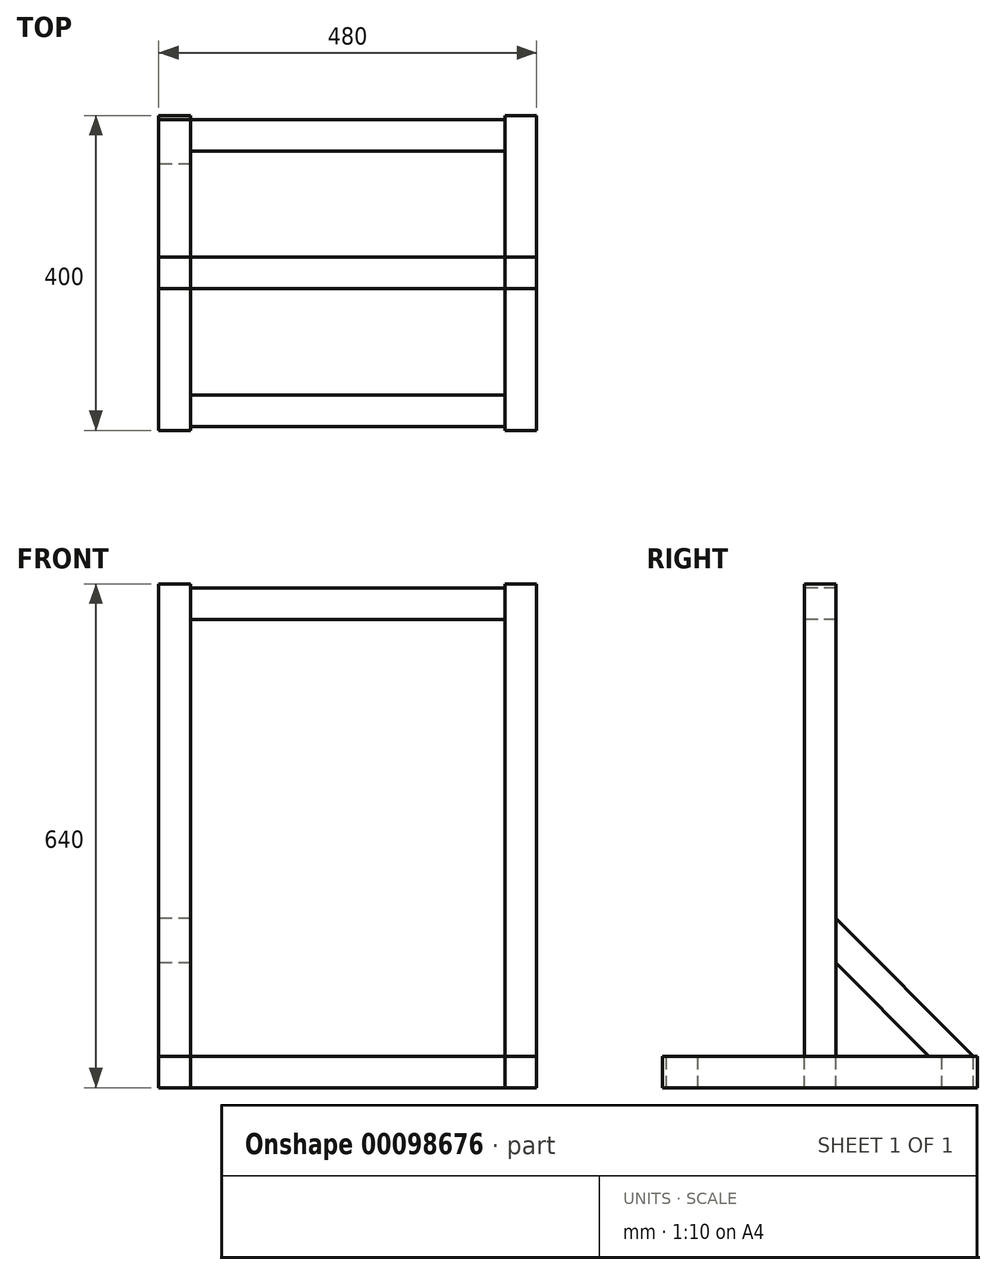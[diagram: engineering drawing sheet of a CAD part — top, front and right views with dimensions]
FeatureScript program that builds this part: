
annotation { "Feature Type Name" : "Feature", "Feature Type Description" : "" }
export const myFeature = defineFeature(function(context is Context, id is Id, definition is map)
    precondition{}
    {
        {
            assignVariable(context, id + "F0", {"name" : "height", "anyValue" : 600});
        }
        {
            var Q0;
            Q0=qCreatedBy(makeId("Top.planeOp"),FACE);
            var sketch = newSketch(context, id + "F1", { "sketchPlane" : qUnion([Q0])});
            skLineSegment(sketch, "E0.bottom", {"start": v(-240, 200) * mm, "end": v(-200, 200) * mm});
            skLineSegment(sketch, "E0.top", {"start": v(-240, -200) * mm, "end": v(-200, -200) * mm});
            skLineSegment(sketch, "E0.left", {"start": v(-240, 200) * mm, "end": v(-240, -200) * mm});
            skLineSegment(sketch, "E0.right", {"start": v(-200, 200) * mm, "end": v(-200, -200) * mm});
            skLineSegment(sketch, "E1", {"start": v(-200, 20) * mm, "end": v(0, 20) * mm});
            skLineSegment(sketch, "E2", {"start": v(-200, -20) * mm, "end": v(0, -20) * mm});
            skLineSegment(sketch, "E3", {"start": v(-200, -155) * mm, "end": v(0, -155) * mm});
            skLineSegment(sketch, "E4", {"start": v(-200, -195) * mm, "end": v(0, -195) * mm});
            skLineSegment(sketch, "E5", {"start": v(0, -195) * mm, "end": v(0, 195) * mm, "construction": true});
            skLineSegment(sketch, "E6.MirrorCS", {"start": v(200, -195) * mm, "end": v(0, -195) * mm});
            skLineSegment(sketch, "E7.MirrorCS", {"start": v(200, -155) * mm, "end": v(0, -155) * mm});
            skLineSegment(sketch, "E8.MirrorCS", {"start": v(200, 200) * mm, "end": v(200, -200) * mm});
            skLineSegment(sketch, "E9.MirrorCS", {"start": v(240, 200) * mm, "end": v(240, -200) * mm});
            skLineSegment(sketch, "E10.MirrorCS", {"start": v(240, 200) * mm, "end": v(200, 200) * mm});
            skLineSegment(sketch, "E11.MirrorCS", {"start": v(240, -200) * mm, "end": v(200, -200) * mm});
            skLineSegment(sketch, "E12.MirrorCS", {"start": v(200, -20) * mm, "end": v(0, -20) * mm});
            skLineSegment(sketch, "E13.MirrorCS", {"start": v(200, 20) * mm, "end": v(0, 20) * mm});
            skLineSegment(sketch, "E14", {"start": v(-200, 20) * mm, "end": v(-240, 20) * mm});
            skLineSegment(sketch, "E15", {"start": v(-200, -20) * mm, "end": v(-240, -20) * mm});
            skLineSegment(sketch, "E16.MirrorCS", {"start": v(200, 20) * mm, "end": v(240, 20) * mm});
            skLineSegment(sketch, "E17.MirrorCS", {"start": v(200, -20) * mm, "end": v(240, -20) * mm});
            skLineSegment(sketch, "E18", {"start": v(-240, 0) * mm, "end": v(240, 0) * mm, "construction": true});
            skLineSegment(sketch, "E19.MirrorCS", {"start": v(200, 155) * mm, "end": v(0, 155) * mm});
            skLineSegment(sketch, "E20.MirrorCS", {"start": v(200, 195) * mm, "end": v(0, 195) * mm});
            skLineSegment(sketch, "E21.MirrorCS", {"start": v(-200, 195) * mm, "end": v(0, 195) * mm});
            skLineSegment(sketch, "E22.MirrorCS", {"start": v(-200, 155) * mm, "end": v(0, 155) * mm});
            skSolve(sketch);
        }
        {
            var Q0;
            {var subQ1=sQuery(id+"F1.wireOp",EDGE,"E0.bottom");Q0=makeQuery(id+"F1.imprint","IMPRINT",FACE,{"disambiguationData":[TD([[makeQuery(id+"F1.imprint","IMPRINT",EDGE,{"derivedFrom":subQ1}),-1.0]])]});}
            var Q1;
            Q1=makeQuery(id+"F1.imprint","IMPRINT",FACE,{"disambiguationData":[TD([[makeQuery(id+"F1.imprint","IMPRINT",EDGE,{"derivedFrom":sQuery(id+"F1.wireOp",EDGE,"E9.MirrorCS")}),-1.0]])]});
            var Q2;
            {var subQ0=sQuery(id+"F1.wireOp",EDGE,"E14");Q2=makeQuery(id+"F1.imprint","IMPRINT",FACE,{"disambiguationData":[TD([[makeQuery(id+"F1.imprint","IMPRINT",EDGE,{"derivedFrom":subQ0}),1.0]])]});}
            var Q3;
            {var subQ3=sQuery(id+"F1.wireOp",EDGE,"E0.top");Q3=makeQuery(id+"F1.imprint","IMPRINT",FACE,{"disambiguationData":[TD([[makeQuery(id+"F1.imprint","IMPRINT",EDGE,{"derivedFrom":subQ3}),1.0]])]});}
            var Q4;
            {var subQ2=sQuery(id+"F1.wireOp",EDGE,"E11.MirrorCS");Q4=makeQuery(id+"F1.imprint","IMPRINT",FACE,{"disambiguationData":[TD([[makeQuery(id+"F1.imprint","IMPRINT",EDGE,{"derivedFrom":subQ2}),-1.0]])]});}
            var Q5;
            {var subQ0=sQuery(id+"F1.wireOp",EDGE,"E10.MirrorCS");Q5=makeQuery(id+"F1.imprint","IMPRINT",FACE,{"disambiguationData":[TD([[makeQuery(id+"F1.imprint","IMPRINT",EDGE,{"derivedFrom":subQ0}),1.0]])]});}
            extrude(context, id + "F2", {"entities" : qUnion([Q0, Q1, Q2, Q3, Q4, Q5]), "oppositeDirection" : true, "depth" : 40 * mm});
        }
        {
            var Q0;
            {var subQ4=sQuery(id+"F1.wireOp",EDGE,"E1");Q0=makeQuery(id+"F1.imprint","IMPRINT",FACE,{"disambiguationData":[TD([[makeQuery(id+"F1.imprint","IMPRINT",EDGE,{"derivedFrom":subQ4}),-1.0]])]});}
            var Q1;
            {var subQ2=sQuery(id+"F1.wireOp",EDGE,"E3");Q1=makeQuery(id+"F1.imprint","IMPRINT",FACE,{"disambiguationData":[TD([[makeQuery(id+"F1.imprint","IMPRINT",EDGE,{"derivedFrom":subQ2}),-1.0]])]});}
            var Q2;
            {var subQ4=sQuery(id+"F1.wireOp",EDGE,"E19.MirrorCS");Q2=makeQuery(id+"F1.imprint","IMPRINT",FACE,{"disambiguationData":[TD([[makeQuery(id+"F1.imprint","IMPRINT",EDGE,{"derivedFrom":subQ4}),-1.0]])]});}
            extrude(context, id + "F3", {"entities" : qUnion([Q0, Q1, Q2]), "oppositeDirection" : true, "depth" : 40 * mm});
        }
        {
            var Q0;
            {var subQ0=sQuery(id+"F1.wireOp",EDGE,"E14");Q0=makeQuery(id+"F1.imprint","IMPRINT",FACE,{"disambiguationData":[TD([[makeQuery(id+"F1.imprint","IMPRINT",EDGE,{"derivedFrom":subQ0}),1.0]])]});}
            var Q1;
            {var subQ2=sQuery(id+"F1.wireOp",EDGE,"E16.MirrorCS");Q1=makeQuery(id+"F1.imprint","IMPRINT",FACE,{"disambiguationData":[TD([[makeQuery(id+"F1.imprint","IMPRINT",EDGE,{"derivedFrom":subQ2}),-1.0]])]});}
            extrude(context, id + "F4", {"entities" : qUnion([Q0, Q1]), "depth" : (getVariable(context, 'height')) * mm});
        }
        {
            var Q0;
            Q0=makeQuery(id+"F4.opExtrude","SWEPT_FACE",FACE,{"disambiguationData":[OSD([sQuery(id+"F1.wireOp",EDGE,"E15")])]});
            var sketch = newSketch(context, id + "F5", { "sketchPlane" : qUnion([Q0])});
            skLineSegment(sketch, "E23.bottom", {"start": v(-200, 595) * mm, "end": v(200, 595) * mm});
            skLineSegment(sketch, "E23.top", {"start": v(-200, 555) * mm, "end": v(200, 555) * mm});
            skLineSegment(sketch, "E23.left", {"start": v(-200, 595) * mm, "end": v(-200, 555) * mm});
            skLineSegment(sketch, "E23.right", {"start": v(200, 595) * mm, "end": v(200, 555) * mm});
            skSolve(sketch);
        }
        {
            var Q0;
            Q0=makeQuery(id+"F5.imprint","IMPRINT",FACE,{"disambiguationData":[TD([[makeQuery(id+"F5.imprint","IMPRINT",EDGE,{"derivedFrom":sQuery(id+"F5.wireOp",EDGE,"E23.bottom")}),-1.0]])]});
            extrude(context, id + "F6", {"entities" : qUnion([Q0]), "oppositeDirection" : true, "depth" : 40 * mm});
        }
        {
            var Q0;
            Q0=makeQuery(id+"F2.opExtrude","SWEPT_FACE",FACE,{"disambiguationData":[OSD([sQuery(id+"F1.wireOp",EDGE,"E0.left")])]});
            var sketch = newSketch(context, id + "F7", { "sketchPlane" : qUnion([Q0])});
            skLineSegment(sketch, "E24", {"start": v(-195, 0) * mm, "end": v(-20, 175) * mm});
            skLineSegment(sketch, "E25", {"start": v(-138.43, 0) * mm, "end": v(-20, 118.43) * mm});
            skLineSegment(sketch, "E26", {"start": v(-195, 0) * mm, "end": v(-138.43, 0) * mm});
            skLineSegment(sketch, "E27", {"start": v(-20, 175) * mm, "end": v(-20, 118.43) * mm});
            skSolve(sketch);
        }
        {
            var Q0;
            Q0=makeQuery(id+"F7.imprint","IMPRINT",FACE,{"disambiguationData":[TD([[makeQuery(id+"F7.imprint","IMPRINT",EDGE,{"derivedFrom":sQuery(id+"F7.wireOp",EDGE,"E24")}),-1.0]])]});
            extrude(context, id + "F8", {"entities" : qUnion([Q0]), "oppositeDirection" : true, "depth" : 40 * mm});
        }
    });
